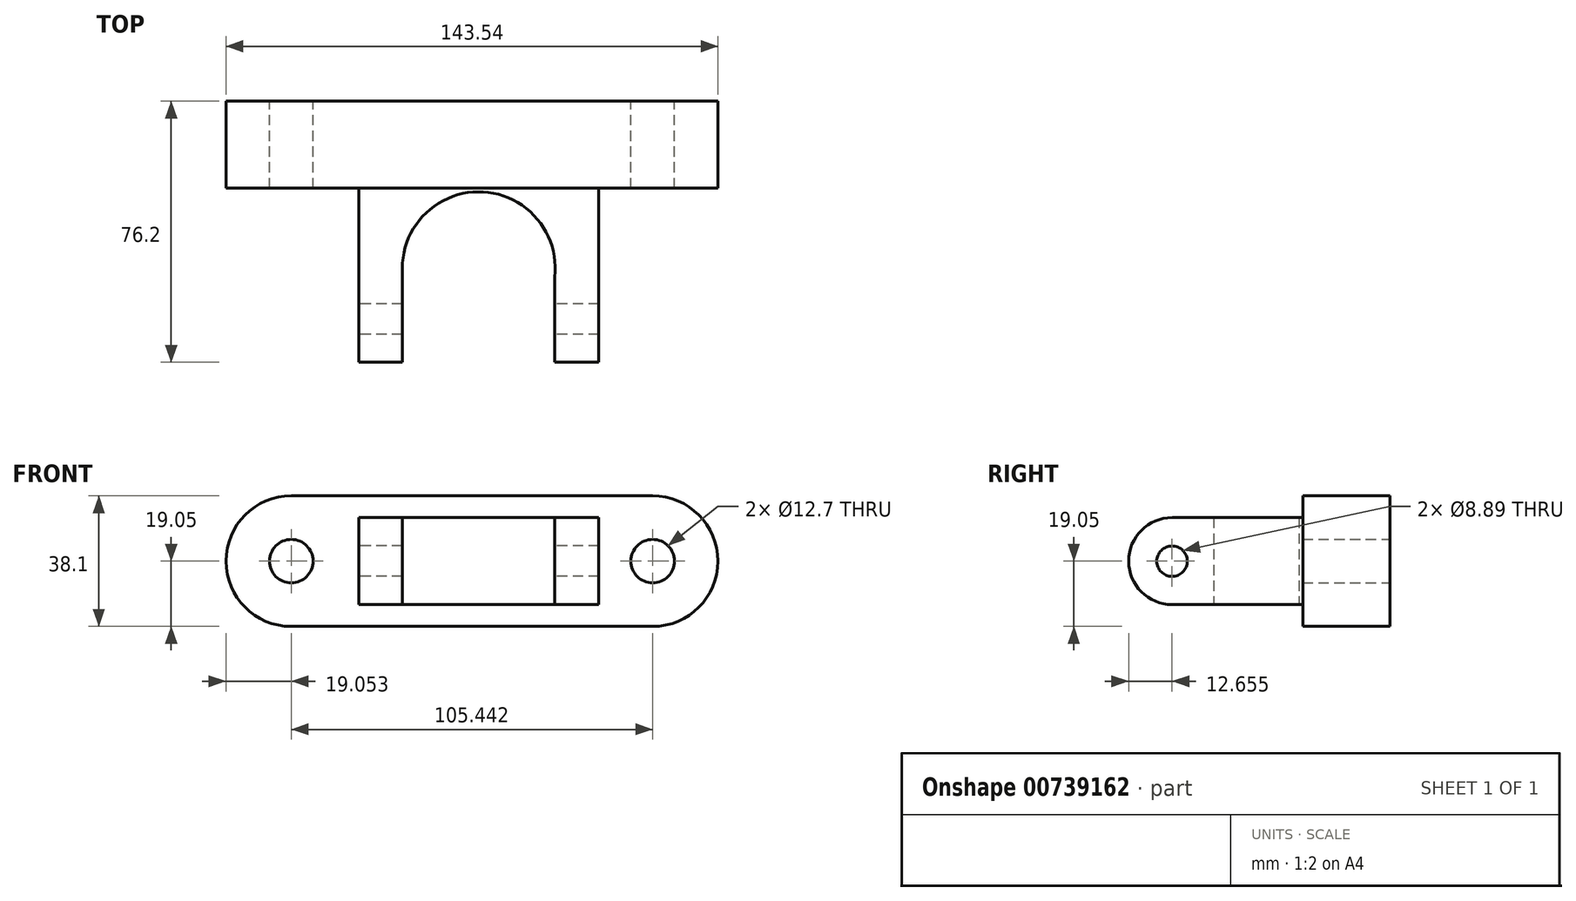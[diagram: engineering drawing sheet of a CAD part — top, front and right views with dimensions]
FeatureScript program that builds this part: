
annotation { "Feature Type Name" : "Feature", "Feature Type Description" : "" }
export const myFeature = defineFeature(function(context is Context, id is Id, definition is map)
    precondition{}
    {
        {
            var Q0;
            Q0=qCreatedBy(makeId("Front.planeOp"),FACE);
            var sketch = newSketch(context, id + "F0", { "sketchPlane" : qUnion([Q0])});
            skLineSegment(sketch, "E0.bottom", {"start": v(50.73, -19.05) * mm, "end": v(-54.7, -19.05) * mm});
            skLineSegment(sketch, "E0.top", {"start": v(50.73, 19.05) * mm, "end": v(-54.7, 19.05) * mm});
            skPoint(sketch, "E0.middle", {"position": v(-1.99, 0) * mm});
            skArc(sketch, "E1", {"start": v(-54.7, 19.05) * mm, "mid": v(-73.76, 0) * mm, "end": v(-54.7, -19.05) * mm});
            skArc(sketch, "E2", {"start": v(50.73, -19.05) * mm, "mid": v(69.78, 0) * mm, "end": v(50.73, 19.05) * mm});
            skCircle(sketch, "E3", {"center": v(-54.7, 0) * mm, "radius": 6.35 * mm});
            skCircle(sketch, "E4", {"center": v(50.73, 0) * mm, "radius": 6.35 * mm});
            skSolve(sketch);
        }
        {
            var Q0;
            Q0=makeQuery(id+"F0.imprint","IMPRINT",FACE,{"disambiguationData":[TD([[makeQuery(id+"F0.imprint","IMPRINT",EDGE,{"derivedFrom":sQuery(id+"F0.wireOp",EDGE,"E0.bottom")}),-1.0]])]});
            extrude(context, id + "F1", {"entities" : qUnion([Q0]), "depth" : 25.4 * mm, "offsetDistance" : 25.4 * mm});
        }
        {
            var Q0;
            Q0=makeQuery(id+"F1.opExtrude","CAP_FACE",FACE,{"disambiguationData":[OSD([sQuery(id+"F0.wireOp",EDGE,"E0.bottom"),sQuery(id+"F0.wireOp",EDGE,"E0.top"),sQuery(id+"F0.wireOp",EDGE,"E1"),sQuery(id+"F0.wireOp",EDGE,"E2"),sQuery(id+"F0.wireOp",EDGE,"E3"),sQuery(id+"F0.wireOp",EDGE,"E4")])],"isStart":false});
            var sketch = newSketch(context, id + "F2", { "sketchPlane" : qUnion([Q0])});
            skLineSegment(sketch, "E5.bottom", {"start": v(35.04, -12.7) * mm, "end": v(-35.04, -12.7) * mm});
            skLineSegment(sketch, "E5.top", {"start": v(35.04, 12.7) * mm, "end": v(-35.04, 12.7) * mm});
            skLineSegment(sketch, "E5.left", {"start": v(35.04, -12.7) * mm, "end": v(35.04, 12.7) * mm});
            skLineSegment(sketch, "E5.right", {"start": v(-35.04, -12.7) * mm, "end": v(-35.04, 12.7) * mm});
            skPoint(sketch, "E5.middle", {"position": v(0, 0) * mm});
            skSolve(sketch);
        }
        {
            var Q0;
            Q0=makeQuery(id+"F2.imprint","IMPRINT",FACE,{"disambiguationData":[TD([[makeQuery(id+"F2.imprint","IMPRINT",EDGE,{"derivedFrom":sQuery(id+"F2.wireOp",EDGE,"E5.bottom")}),-1.0]])]});
            extrude(context, id + "F3", {"entities" : qUnion([Q0]), "operationType" : NewBodyOperationType.ADD, "depth" : 50.8 * mm, "offsetDistance" : 25.4 * mm});
        }
        {
            var Q0;
            Q0=makeQuery(id+"F3.opExtrude","SWEPT_FACE",FACE,{"disambiguationData":[OSD([sQuery(id+"F2.wireOp",EDGE,"E5.bottom")])]});
            var sketch = newSketch(context, id + "F4", { "sketchPlane" : qUnion([Q0])});
            skLineSegment(sketch, "E6.bottom", {"start": v(-22.3, 76.2) * mm, "end": v(22.15, 76.2) * mm});
            skLineSegment(sketch, "E6.left", {"start": v(-22.3, 76.2) * mm, "end": v(-22.3, 48.76) * mm});
            skLineSegment(sketch, "E6.right", {"start": v(22.15, 76.2) * mm, "end": v(22.15, 51.34) * mm});
            skArc(sketch, "E7", {"start": v(-22.3, 48.76) * mm, "mid": v(1.29, 26.5) * mm, "end": v(22.15, 51.34) * mm});
            skSolve(sketch);
        }
        {
            var Q0;
            Q0=makeQuery(id+"F4.imprint","IMPRINT",FACE,{"disambiguationData":[TD([[makeQuery(id+"F4.imprint","IMPRINT",EDGE,{"derivedFrom":sQuery(id+"F4.wireOp",EDGE,"E6.bottom")}),1.0]])]});
            extrude(context, id + "F5", {"entities" : qUnion([Q0]), "operationType" : NewBodyOperationType.REMOVE, "oppositeDirection" : true, "depth" : 25.4 * mm, "offsetDistance" : 25.4 * mm});
        }
        {
            var Q0;
            Q0=makeQuery(id+"F3.opExtrude","SWEPT_FACE",FACE,{"disambiguationData":[OSD([sQuery(id+"F2.wireOp",EDGE,"E5.right")])]});
            var sketch = newSketch(context, id + "F6", { "sketchPlane" : qUnion([Q0])});
            skCircle(sketch, "E8", {"center": v(63.55, 0) * mm, "radius": 4.45 * mm});
            skSolve(sketch);
        }
        {
            var Q0;
            Q0=makeQuery(id+"F6.imprint","IMPRINT",FACE,{"disambiguationData":[TD([[makeQuery(id+"F6.imprint","IMPRINT",EDGE,{"derivedFrom":sQuery(id+"F6.wireOp",EDGE,"E8")}),1.0]])]});
            extrude(context, id + "F7", {"entities" : qUnion([Q0]), "operationType" : NewBodyOperationType.REMOVE, "oppositeDirection" : true, "depth" : 127 * mm, "offsetDistance" : 25.4 * mm});
        }
        {
            var Q0;
            {var subQ0=sQuery(id+"F2.wireOp",EDGE,"E5.right");var subQ1=sQuery(id+"F2.wireOp",EDGE,"E5.top");Q0=makeQuery(id+"F5.boolean.opBoolean","SPLIT",EDGE,{"disambiguationData":[TD([makeQuery(id+"F3.opExtrude","SWEPT_FACE",FACE,{"disambiguationData":[OSD([subQ0])]})])],"derivedFrom":makeQuery(id+"F3.opExtrude","CAP_EDGE",EDGE,{"disambiguationData":[OSD([subQ1])],"isStart":false})});}
            var Q1;
            {var subQ0=sQuery(id+"F2.wireOp",EDGE,"E5.bottom");var subQ1=sQuery(id+"F2.wireOp",EDGE,"E5.right");Q1=makeQuery(id+"F5.boolean.opBoolean","SPLIT",EDGE,{"disambiguationData":[TD([makeQuery(id+"F3.opExtrude","SWEPT_FACE",FACE,{"disambiguationData":[OSD([subQ1])]})])],"derivedFrom":makeQuery(id+"F3.opExtrude","CAP_EDGE",EDGE,{"disambiguationData":[OSD([subQ0])],"isStart":false})});}
            var Q2;
            {var subQ0=sQuery(id+"F2.wireOp",EDGE,"E5.left");var subQ1=sQuery(id+"F2.wireOp",EDGE,"E5.top");Q2=makeQuery(id+"F5.boolean.opBoolean","SPLIT",EDGE,{"disambiguationData":[TD([makeQuery(id+"F3.opExtrude","SWEPT_FACE",FACE,{"disambiguationData":[OSD([subQ0])]})])],"derivedFrom":makeQuery(id+"F3.opExtrude","CAP_EDGE",EDGE,{"disambiguationData":[OSD([subQ1])],"isStart":false})});}
            var Q3;
            {var subQ0=sQuery(id+"F2.wireOp",EDGE,"E5.bottom");var subQ1=sQuery(id+"F2.wireOp",EDGE,"E5.left");Q3=makeQuery(id+"F5.boolean.opBoolean","SPLIT",EDGE,{"disambiguationData":[TD([makeQuery(id+"F3.opExtrude","SWEPT_FACE",FACE,{"disambiguationData":[OSD([subQ1])]})])],"derivedFrom":makeQuery(id+"F3.opExtrude","CAP_EDGE",EDGE,{"disambiguationData":[OSD([subQ0])],"isStart":false})});}
            fillet(context, id + "F8", {"entities" : qUnion([Q0, Q1, Q2, Q3]), "radius" : 12.7 * mm, "tangentPropagation" : true, "allowEdgeOverflow" : false});
        }
    });
